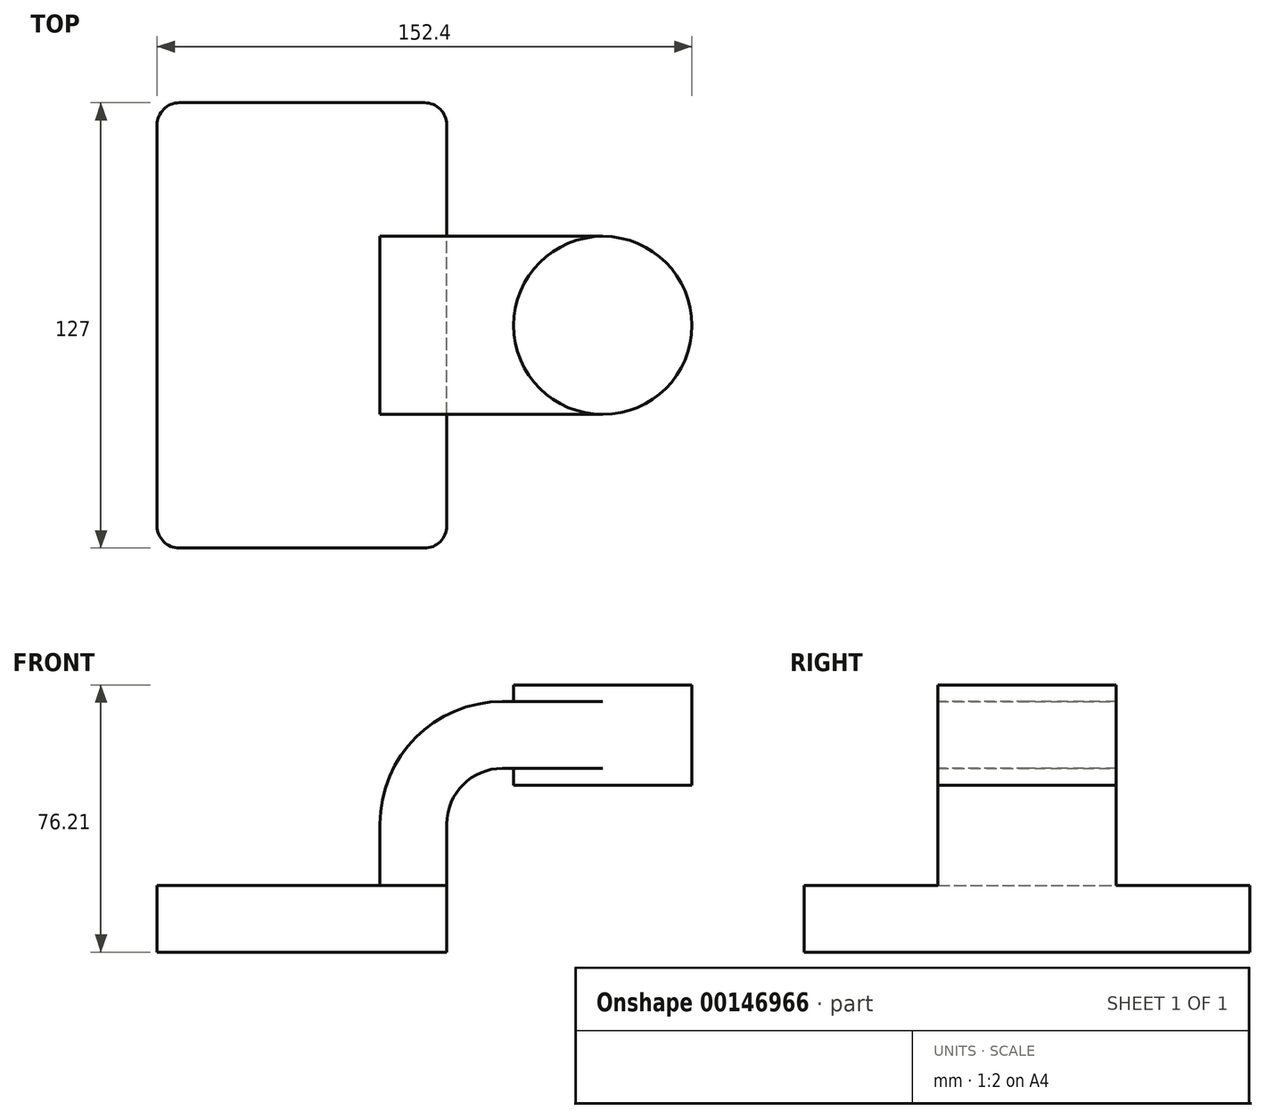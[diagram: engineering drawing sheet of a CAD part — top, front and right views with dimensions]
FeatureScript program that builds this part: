
annotation { "Feature Type Name" : "Feature", "Feature Type Description" : "" }
export const myFeature = defineFeature(function(context is Context, id is Id, definition is map)
    precondition{}
    {
        {
            var Q0;
            Q0=qCreatedBy(makeId("Front.planeOp"),FACE);
            var sketch = newSketch(context, id + "F0", { "sketchPlane" : qUnion([Q0])});
            skLineSegment(sketch, "E0.bottom", {"start": v(-41.28, 9.52) * mm, "end": v(41.27, 9.53) * mm});
            skLineSegment(sketch, "E0.top", {"start": v(-41.27, -9.53) * mm, "end": v(41.28, -9.53) * mm});
            skLineSegment(sketch, "E0.left", {"start": v(-41.28, 9.52) * mm, "end": v(-41.27, -9.53) * mm});
            skLineSegment(sketch, "E0.right", {"start": v(41.28, 9.53) * mm, "end": v(41.28, -9.52) * mm});
            skPoint(sketch, "E0.middle", {"position": v(0, 0) * mm});
            skLineSegment(sketch, "E1.bottom", {"start": v(60.33, 66.67) * mm, "end": v(111.12, 66.67) * mm});
            skLineSegment(sketch, "E1.top", {"start": v(60.33, 38.1) * mm, "end": v(111.12, 38.1) * mm});
            skLineSegment(sketch, "E1.left", {"start": v(60.33, 66.68) * mm, "end": v(60.33, 38.1) * mm});
            skLineSegment(sketch, "E1.right", {"start": v(111.13, 66.68) * mm, "end": v(111.13, 38.1) * mm});
            skLineSegment(sketch, "E2", {"start": v(41.27, 9.53) * mm, "end": v(41.27, 27) * mm});
            skArc(sketch, "E3", {"start": v(41.27, 27) * mm, "mid": v(45.92, 38.23) * mm, "end": v(57.15, 42.88) * mm});
            skLineSegment(sketch, "E4", {"start": v(57.15, 42.88) * mm, "end": v(85.72, 42.88) * mm});
            skPoint(sketch, "E4.endSnap0", {"position": v(85.72, 38.1) * mm});
            skLineSegment(sketch, "E5.0", {"start": v(57.15, 61.93) * mm, "end": v(85.72, 61.93) * mm});
            skArc(sketch, "E5.1", {"start": v(22.22, 27) * mm, "mid": v(32.45, 51.7) * mm, "end": v(57.15, 61.93) * mm});
            skLineSegment(sketch, "E5.2", {"start": v(22.22, 9.53) * mm, "end": v(22.22, 27) * mm});
            skLineSegment(sketch, "E6", {"start": v(85.72, 38.1) * mm, "end": v(85.72, 66.67) * mm});
            skFitSpline(sketch, "E7", {"points": [v(-41.28, 9.53) * mm, v(57.15, 61.93) * mm], "startDerivative": vector(4.57, 106.3) * mm, "endDerivative": vector(173.83, -3.9) * mm});
            skSolve(sketch);
        }
        {
            var Q0;
            Q0=makeQuery(id+"F0.imprint","IMPRINT",FACE,{"disambiguationData":[TD([[makeQuery(id+"F0.imprint","IMPRINT",EDGE,{"derivedFrom":sQuery(id+"F0.wireOp",EDGE,"E0.top")}),1.0]])]});
            extrude(context, id + "F1", {"entities" : qUnion([Q0]), "endBound" : BoundingType.SYMMETRIC, "depth" : 127 * mm});
        }
        {
            var Q0;
            {var subQ1=sQuery(id+"F0.wireOp",EDGE,"E2");Q0=makeQuery(id+"F0.imprint","IMPRINT",FACE,{"disambiguationData":[TD([[makeQuery(id+"F0.imprint","IMPRINT",EDGE,{"derivedFrom":subQ1}),1.0]])]});}
            var Q1;
            {var subQ0=sQuery(id+"F0.wireOp",EDGE,"E5.0");var subQ1=sQuery(id+"F0.wireOp",EDGE,"E1.left");var subQ2=makeQuery(id+"F0.imprint","INTERSECT",VERTEX,{"derivedFrom":[subQ1,subQ0]});Q1=makeQuery(id+"F0.imprint","IMPRINT",FACE,{"disambiguationData":[TD([[makeQuery(id+"F0.imprint","IMPRINT",EDGE,{"disambiguationData":[TD([[subQ2,-1.0]])],"derivedFrom":subQ1}),1.0]])]});}
            extrude(context, id + "F2", {"entities" : qUnion([Q0, Q1]), "operationType" : NewBodyOperationType.ADD, "endBound" : BoundingType.SYMMETRIC, "depth" : 50.8 * mm});
        }
        {
            var Q0;
            Q0=makeQuery(id+"F0.imprint","IMPRINT",FACE,{"disambiguationData":[TD([[makeQuery(id+"F0.imprint","IMPRINT",EDGE,{"derivedFrom":sQuery(id+"F0.wireOp",EDGE,"E5.1")}),1.0]])]});
            extrude(context, id + "F3", {"entities" : qUnion([Q0]), "operationType" : NewBodyOperationType.ADD, "endBound" : BoundingType.SYMMETRIC, "depth" : 15.88 * mm});
        }
        {
            var Q0;
            {var subQ0=sQuery(id+"F0.wireOp",EDGE,"E1.right");Q0=makeQuery(id+"F0.imprint","IMPRINT",FACE,{"disambiguationData":[TD([[makeQuery(id+"F0.imprint","IMPRINT",EDGE,{"derivedFrom":subQ0}),-1.0]])]});}
            var Q1;
            Q1=sQuery(id+"F0.wireOp",EDGE,"E6");
            revolve(context, id + "F4", {"operationType" : NewBodyOperationType.ADD, "entities" : qUnion([Q0]), "axis" : qUnion([Q1]), "revolveType" : RevolveType.FULL});
        }
        {
            var Q0;
            Q0=makeQuery(id+"F1.opExtrude","CAP_EDGE",EDGE,{"disambiguationData":[OSD([sQuery(id+"F0.wireOp",EDGE,"E0.left")])],"isStart":false});
            var Q1;
            Q1=makeQuery(id+"F1.opExtrude","CAP_EDGE",EDGE,{"disambiguationData":[OSD([sQuery(id+"F0.wireOp",EDGE,"E0.right")])],"isStart":false});
            var Q2;
            Q2=makeQuery(id+"F1.opExtrude","CAP_EDGE",EDGE,{"disambiguationData":[OSD([sQuery(id+"F0.wireOp",EDGE,"E0.right")])],"isStart":true});
            var Q3;
            Q3=makeQuery(id+"F1.opExtrude","CAP_EDGE",EDGE,{"disambiguationData":[OSD([sQuery(id+"F0.wireOp",EDGE,"E0.left")])],"isStart":true});
            fillet(context, id + "F5", {"entities" : qUnion([Q0, Q1, Q2, Q3]), "radius" : 6.35 * mm, "tangentPropagation" : true, "allowEdgeOverflow" : false});
        }
    });
